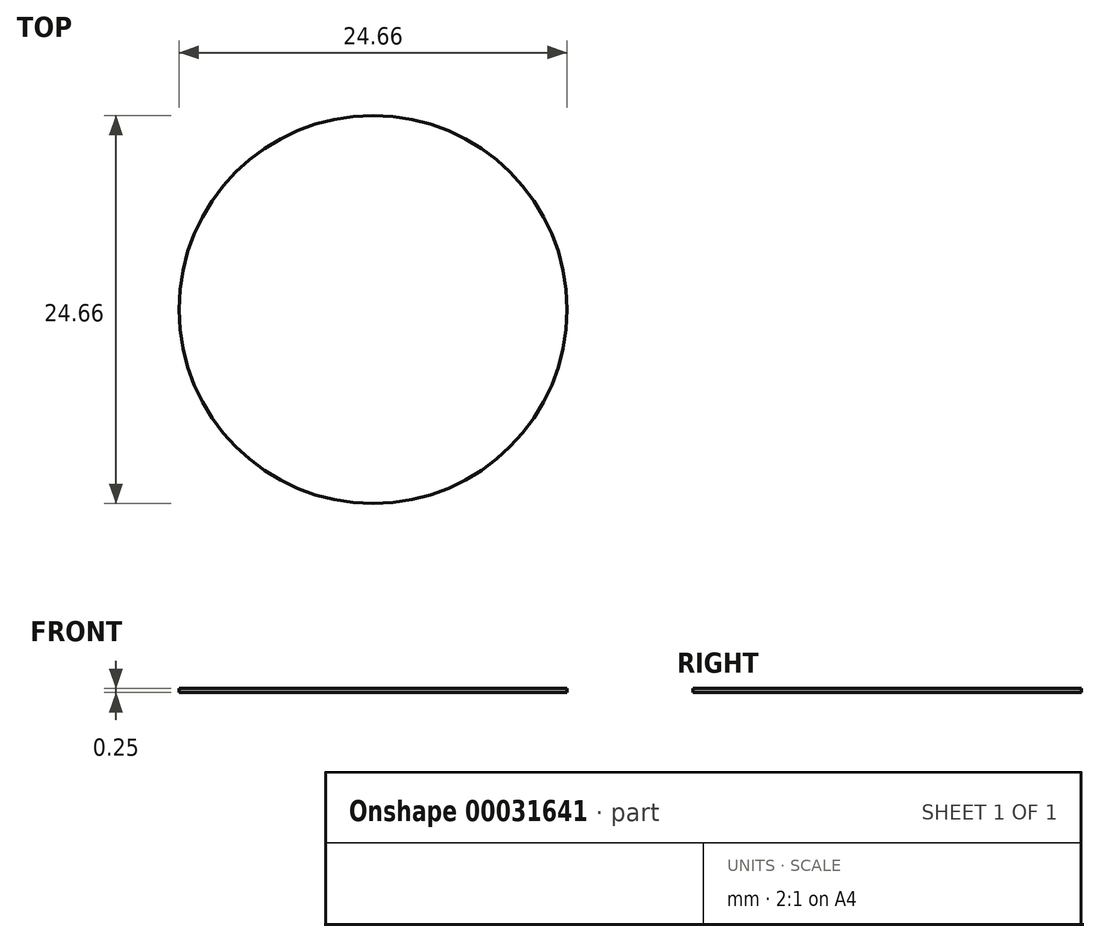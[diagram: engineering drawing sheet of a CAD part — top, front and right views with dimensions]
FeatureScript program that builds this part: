
annotation { "Feature Type Name" : "Feature", "Feature Type Description" : "" }
export const myFeature = defineFeature(function(context is Context, id is Id, definition is map)
    precondition{}
    {
        {
            var Q0;
            Q0=qCreatedBy(makeId("Top.planeOp"),FACE);
            var sketch = newSketch(context, id + "F0", { "sketchPlane" : qUnion([Q0])});
            skCircle(sketch, "E0", {"center": v(0, 0) * mm, "radius": 12.32 * mm});
            skSolve(sketch);
        }
        {
            var Q0;
            Q0 = qSketchRegion(id + "F0", true);
            extrude(context, id + "F1", {"entities" : qUnion([Q0]), "depth" : .25 * mm});
        }
    });
